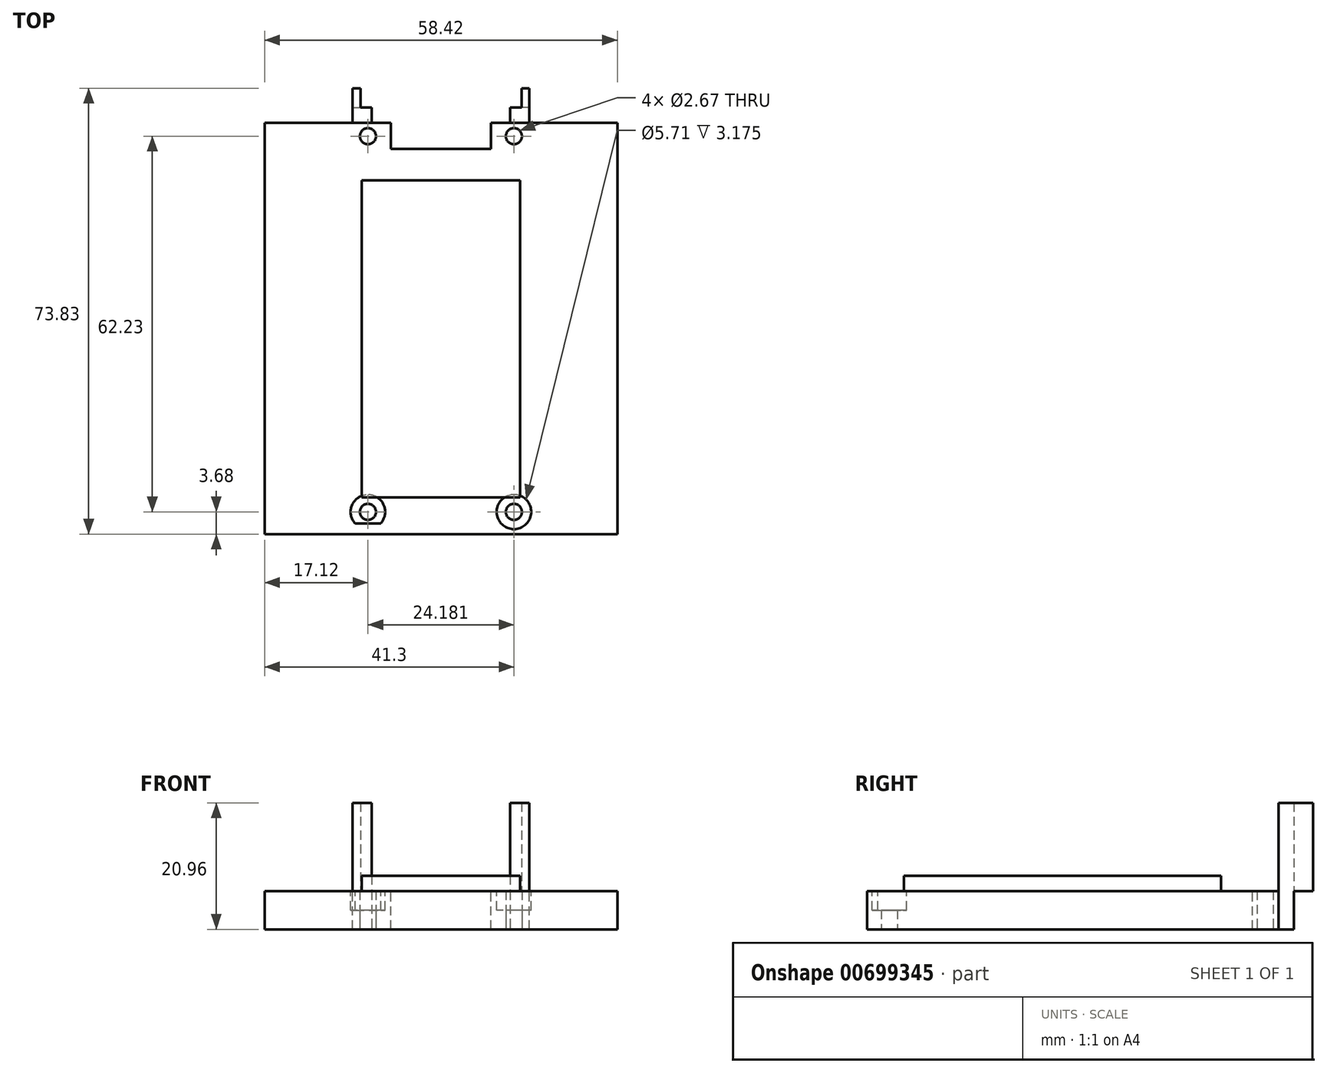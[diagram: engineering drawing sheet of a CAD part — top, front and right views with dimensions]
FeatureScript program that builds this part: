
annotation { "Feature Type Name" : "Feature", "Feature Type Description" : "" }
export const myFeature = defineFeature(function(context is Context, id is Id, definition is map)
    precondition{}
    {
        {
            var Q0;
            Q0=qCreatedBy(makeId("Top.planeOp"),FACE);
            var sketch = newSketch(context, id + "F0", { "sketchPlane" : qUnion([Q0])});
            skLineSegment(sketch, "E0.bottom", {"start": v(0, 0) * mm, "end": v(58.42, 0) * mm});
            skLineSegment(sketch, "E0.top", {"start": v(0, -66.34) * mm, "end": v(58.42, -66.34) * mm});
            skLineSegment(sketch, "E0.left", {"start": v(0, 0) * mm, "end": v(0, -66.34) * mm});
            skLineSegment(sketch, "E0.right", {"start": v(58.42, 0) * mm, "end": v(58.42, -66.34) * mm});
            skCircle(sketch, "E1", {"center": v(41.3, -64.44) * mm, "radius": 1.33 * mm});
            skCircle(sketch, "E2", {"center": v(17.12, -64.44) * mm, "radius": 1.33 * mm});
            skCircle(sketch, "E3", {"center": v(41.3, -2.2) * mm, "radius": 1.33 * mm});
            skCircle(sketch, "E4", {"center": v(17.12, -2.2) * mm, "radius": 1.33 * mm});
            skCircle(sketch, "E5", {"center": v(17.12, -64.44) * mm, "radius": 2.86 * mm});
            skCircle(sketch, "E6", {"center": v(41.3, -64.44) * mm, "radius": 2.86 * mm});
            skSolve(sketch);
        }
        {
            var Q0;
            Q0=makeQuery(id+"F0.imprint","IMPRINT",FACE,{"disambiguationData":[TD([[makeQuery(id+"F0.imprint","IMPRINT",EDGE,{"derivedFrom":sQuery(id+"F0.wireOp",EDGE,"E0.bottom")}),-1.0]])]});
            var Q1;
            Q1=makeQuery(id+"F0.imprint","IMPRINT",FACE,{"disambiguationData":[TD([[makeQuery(id+"F0.imprint","IMPRINT",EDGE,{"derivedFrom":sQuery(id+"F0.wireOp",EDGE,"E2")}),-1.0]])]});
            var Q2;
            Q2=makeQuery(id+"F0.imprint","IMPRINT",FACE,{"disambiguationData":[TD([[makeQuery(id+"F0.imprint","IMPRINT",EDGE,{"derivedFrom":sQuery(id+"F0.wireOp",EDGE,"E1")}),-1.0]])]});
            extrude(context, id + "F1", {"entities" : qUnion([Q0, Q1, Q2]), "depth" : 6.35 * mm, "offsetDistance" : 25.4 * mm});
        }
        {
            var Q0;
            Q0=makeQuery(id+"F1.opExtrude","CAP_FACE",FACE,{"disambiguationData":[OSD([sQuery(id+"F0.wireOp",EDGE,"E0.bottom"),sQuery(id+"F0.wireOp",EDGE,"E0.top"),sQuery(id+"F0.wireOp",EDGE,"E0.left"),sQuery(id+"F0.wireOp",EDGE,"E0.right"),sQuery(id+"F0.wireOp",EDGE,"E1"),sQuery(id+"F0.wireOp",EDGE,"E2"),sQuery(id+"F0.wireOp",EDGE,"E3"),sQuery(id+"F0.wireOp",EDGE,"E4")])],"isStart":false});
            var sketch = newSketch(context, id + "F2", { "sketchPlane" : qUnion([Q0])});
            skLineSegment(sketch, "E7.bottom", {"start": v(37.46, -4.32) * mm, "end": v(20.96, -4.32) * mm});
            skLineSegment(sketch, "E7.top", {"start": v(37.46, 0) * mm, "end": v(20.96, 0) * mm});
            skLineSegment(sketch, "E7.left", {"start": v(37.46, -4.32) * mm, "end": v(37.46, 0) * mm});
            skLineSegment(sketch, "E7.right", {"start": v(20.96, -4.32) * mm, "end": v(20.96, 0) * mm});
            skLineSegment(sketch, "E8.bottom", {"start": v(0, 0) * mm, "end": v(20.96, 0) * mm});
            skLineSegment(sketch, "E8.top", {"start": v(0, -4.32) * mm, "end": v(20.96, -4.32) * mm});
            skLineSegment(sketch, "E8.left", {"start": v(0, 0) * mm, "end": v(0, -4.32) * mm});
            skLineSegment(sketch, "E8.right", {"start": v(20.96, 0) * mm, "end": v(20.96, -4.32) * mm});
            skLineSegment(sketch, "E9.bottom", {"start": v(37.46, 0) * mm, "end": v(58.42, 0) * mm});
            skLineSegment(sketch, "E9.top", {"start": v(37.46, -4.32) * mm, "end": v(58.42, -4.32) * mm});
            skLineSegment(sketch, "E9.left", {"start": v(37.46, 0) * mm, "end": v(37.46, -4.32) * mm});
            skLineSegment(sketch, "E9.right", {"start": v(58.42, 0) * mm, "end": v(58.42, -4.32) * mm});
            skLineSegment(sketch, "E10.bottom", {"start": v(20.96, 0) * mm, "end": v(13.3, 0) * mm});
            skLineSegment(sketch, "E10.top", {"start": v(20.96, -4.32) * mm, "end": v(13.3, -4.32) * mm});
            skLineSegment(sketch, "E10.right", {"start": v(13.3, 0) * mm, "end": v(13.3, -4.32) * mm});
            skLineSegment(sketch, "E11.bottom", {"start": v(37.46, 0) * mm, "end": v(45.12, 0) * mm});
            skLineSegment(sketch, "E11.top", {"start": v(37.46, -4.32) * mm, "end": v(45.12, -4.32) * mm});
            skLineSegment(sketch, "E11.right", {"start": v(45.12, 0) * mm, "end": v(45.12, -4.32) * mm});
            skLineSegment(sketch, "E12.bottom", {"start": v(20.96, 0) * mm, "end": v(19.56, 0) * mm});
            skLineSegment(sketch, "E12.top", {"start": v(20.96, -4.32) * mm, "end": v(19.56, -4.32) * mm});
            skLineSegment(sketch, "E12.right", {"start": v(19.56, 0) * mm, "end": v(19.56, -4.32) * mm});
            skLineSegment(sketch, "E13.bottom", {"start": v(37.46, 0) * mm, "end": v(38.86, 0) * mm});
            skLineSegment(sketch, "E13.top", {"start": v(37.46, -4.32) * mm, "end": v(38.86, -4.32) * mm});
            skLineSegment(sketch, "E13.right", {"start": v(38.86, 0) * mm, "end": v(38.86, -4.32) * mm});
            skSolve(sketch);
        }
        {
            var Q0;
            Q0=makeQuery(id+"F2.imprint","IMPRINT",FACE,{"disambiguationData":[TD([[makeQuery(id+"F2.imprint","IMPRINT",EDGE,{"derivedFrom":sQuery(id+"F2.wireOp",EDGE,"E7.bottom")}),-1.0]])]});
            extrude(context, id + "F3", {"entities" : qUnion([Q0]), "operationType" : NewBodyOperationType.REMOVE, "endBound" : BoundingType.THROUGH_ALL, "oppositeDirection" : true, "depth" : 25.4 * mm, "offsetDistance" : 25.4 * mm});
        }
        {
            var Q0;
            Q0=makeQuery(id+"F1.opExtrude","CAP_FACE",FACE,{"disambiguationData":[OSD([sQuery(id+"F0.wireOp",EDGE,"E0.bottom"),sQuery(id+"F0.wireOp",EDGE,"E0.top"),sQuery(id+"F0.wireOp",EDGE,"E0.left"),sQuery(id+"F0.wireOp",EDGE,"E0.right"),sQuery(id+"F0.wireOp",EDGE,"E1"),sQuery(id+"F0.wireOp",EDGE,"E2"),sQuery(id+"F0.wireOp",EDGE,"E3"),sQuery(id+"F0.wireOp",EDGE,"E4")])],"isStart":false});
            var sketch = newSketch(context, id + "F4", { "sketchPlane" : qUnion([Q0])});
            skLineSegment(sketch, "E14.bottom", {"start": v(16.13, -4.32) * mm, "end": v(42.3, -4.32) * mm});
            skLineSegment(sketch, "E14.top", {"start": v(16.13, -62.03) * mm, "end": v(42.3, -62.03) * mm});
            skLineSegment(sketch, "E14.left", {"start": v(16.13, -4.32) * mm, "end": v(16.13, -62.03) * mm});
            skLineSegment(sketch, "E14.right", {"start": v(42.3, -4.32) * mm, "end": v(42.3, -62.03) * mm});
            skLineSegment(sketch, "E15.bottom", {"start": v(16.13, -4.32) * mm, "end": v(21.34, -4.32) * mm});
            skLineSegment(sketch, "E15.top", {"start": v(16.13, -62.03) * mm, "end": v(21.34, -62.03) * mm});
            skLineSegment(sketch, "E15.right", {"start": v(21.34, -4.32) * mm, "end": v(21.34, -62.03) * mm});
            skLineSegment(sketch, "E16.top", {"start": v(16.13, -9.52) * mm, "end": v(42.3, -9.52) * mm});
            skLineSegment(sketch, "E16.left", {"start": v(16.13, -4.32) * mm, "end": v(16.13, -9.52) * mm});
            skLineSegment(sketch, "E16.right", {"start": v(42.3, -4.32) * mm, "end": v(42.3, -9.52) * mm});
            skLineSegment(sketch, "E17.bottom", {"start": v(42.3, -4.32) * mm, "end": v(37.08, -4.32) * mm});
            skLineSegment(sketch, "E17.top", {"start": v(42.3, -62.03) * mm, "end": v(37.08, -62.03) * mm});
            skLineSegment(sketch, "E17.right", {"start": v(37.08, -4.32) * mm, "end": v(37.08, -62.03) * mm});
            skSolve(sketch);
        }
        {
            var Q0;
            Q0=makeQuery(id+"F1.opExtrude","SWEPT_FACE",FACE,{"disambiguationData":[OSD([sQuery(id+"F0.wireOp",EDGE,"E0.top")])]});
            extrude(context, id + "F5", {"entities" : qUnion([Q0]), "operationType" : NewBodyOperationType.ADD, "depth" : 1.78 * mm, "offsetDistance" : 25.4 * mm});
        }
        {
            var Q0;
            Q0=makeQuery(id+"F0.imprint","IMPRINT",FACE,{"disambiguationData":[TD([[makeQuery(id+"F0.imprint","IMPRINT",EDGE,{"derivedFrom":sQuery(id+"F0.wireOp",EDGE,"E1")}),-1.0]])]});
            var Q1;
            Q1=makeQuery(id+"F0.imprint","IMPRINT",FACE,{"disambiguationData":[TD([[makeQuery(id+"F0.imprint","IMPRINT",EDGE,{"derivedFrom":sQuery(id+"F0.wireOp",EDGE,"E2")}),-1.0]])]});
            var Q2;
            {var subQ0=sQuery(id+"F0.wireOp",EDGE,"E5");var subQ1=sQuery(id+"F0.wireOp",EDGE,"E0.top");var subQ2=makeQuery(id+"F0.imprint","INTERSECT",VERTEX,{"disambiguationData":[OD(0.0)],"derivedFrom":[subQ1,subQ0]});Q2=makeQuery(id+"F0.imprint","IMPRINT",FACE,{"disambiguationData":[TD([[makeQuery(id+"F0.imprint","IMPRINT",EDGE,{"disambiguationData":[TD([[subQ2,-1.0]])],"derivedFrom":subQ1}),-1.0]])]});}
            var Q3;
            {var subQ0=sQuery(id+"F0.wireOp",EDGE,"E6");var subQ1=sQuery(id+"F0.wireOp",EDGE,"E0.top");var subQ2=makeQuery(id+"F0.imprint","INTERSECT",VERTEX,{"disambiguationData":[OD(0.0)],"derivedFrom":[subQ1,subQ0]});Q3=makeQuery(id+"F0.imprint","IMPRINT",FACE,{"disambiguationData":[TD([[makeQuery(id+"F0.imprint","IMPRINT",EDGE,{"disambiguationData":[TD([[subQ2,-1.0]])],"derivedFrom":subQ1}),-1.0]])]});}
            extrude(context, id + "F6", {"entities" : qUnion([Q0, Q1, Q2, Q3]), "operationType" : NewBodyOperationType.ADD, "depth" : 6.6 * mm, "offsetDistance" : 25.4 * mm});
        }
        {
            var Q0;
            Q0=makeQuery(id+"F6.opExtrude","CAP_FACE",FACE,{"disambiguationData":[OSD([sQuery(id+"F0.wireOp",EDGE,"E2"),sQuery(id+"F0.wireOp",EDGE,"E5")])],"isStart":false});
            var Q1;
            Q1=makeQuery(id+"F6.opExtrude","CAP_FACE",FACE,{"disambiguationData":[OSD([sQuery(id+"F0.wireOp",EDGE,"E1"),sQuery(id+"F0.wireOp",EDGE,"E6")])],"isStart":false});
            extrude(context, id + "F7", {"entities" : qUnion([Q0, Q1]), "operationType" : NewBodyOperationType.REMOVE, "oppositeDirection" : true, "depth" : 3.43 * mm, "offsetDistance" : 25.4 * mm});
        }
        {
            var Q0;
            {var subQ0=sQuery(id+"F4.wireOp",EDGE,"E14.top");Q0=makeQuery(id+"F4.imprint","IMPRINT",FACE,{"disambiguationData":[TD([[makeQuery(id+"F4.imprint","IMPRINT",EDGE,{"derivedFrom":subQ0}),1.0]])]});}
            extrude(context, id + "F8", {"entities" : qUnion([Q0]), "operationType" : NewBodyOperationType.ADD, "depth" : 2.54 * mm, "offsetDistance" : 25.4 * mm});
        }
        {
            var Q0;
            {var subQ5=sQuery(id+"F0.wireOp",EDGE,"E0.left");var subQ7=sQuery(id+"F0.wireOp",EDGE,"E0.bottom");Q0=makeQuery(id+"F3.boolean.opBoolean","SPLIT",FACE,{"disambiguationData":[TD([makeQuery(id+"F1.opExtrude","SWEPT_FACE",FACE,{"disambiguationData":[OSD([subQ5])]})])],"derivedFrom":makeQuery(id+"F1.opExtrude","SWEPT_FACE",FACE,{"disambiguationData":[OSD([subQ7])]})});}
            var sketch = newSketch(context, id + "F9", { "sketchPlane" : qUnion([Q0])});
            skLineSegment(sketch, "E18.bottom", {"start": v(-20.96, 0) * mm, "end": v(-14.6, 0) * mm});
            skLineSegment(sketch, "E18.top", {"start": v(-20.96, 6.35) * mm, "end": v(-14.6, 6.35) * mm});
            skLineSegment(sketch, "E18.left", {"start": v(-20.96, 0) * mm, "end": v(-20.96, 6.35) * mm});
            skLineSegment(sketch, "E18.right", {"start": v(-14.6, 0) * mm, "end": v(-14.6, 6.35) * mm});
            skSolve(sketch);
        }
        {
            var Q0;
            {var subQ4=sQuery(id+"F0.wireOp",EDGE,"E0.right");var subQ7=sQuery(id+"F0.wireOp",EDGE,"E0.bottom");Q0=makeQuery(id+"F3.boolean.opBoolean","SPLIT",FACE,{"disambiguationData":[TD([makeQuery(id+"F1.opExtrude","SWEPT_FACE",FACE,{"disambiguationData":[OSD([subQ4])]})])],"derivedFrom":makeQuery(id+"F1.opExtrude","SWEPT_FACE",FACE,{"disambiguationData":[OSD([subQ7])]})});}
            var sketch = newSketch(context, id + "F10", { "sketchPlane" : qUnion([Q0])});
            skLineSegment(sketch, "E19.bottom", {"start": v(-37.46, 0) * mm, "end": v(-43.81, 0) * mm});
            skLineSegment(sketch, "E19.top", {"start": v(-37.46, 6.35) * mm, "end": v(-43.81, 6.35) * mm});
            skLineSegment(sketch, "E19.left", {"start": v(-37.46, 0) * mm, "end": v(-37.46, 6.35) * mm});
            skLineSegment(sketch, "E19.right", {"start": v(-43.81, 0) * mm, "end": v(-43.81, 6.35) * mm});
            skSolve(sketch);
        }
        {
            var Q0;
            Q0=makeQuery(id+"F9.imprint","IMPRINT",FACE,{"disambiguationData":[TD([[makeQuery(id+"F9.imprint","IMPRINT",EDGE,{"derivedFrom":sQuery(id+"F9.wireOp",EDGE,"E18.bottom")}),-1.0]])]});
            var Q1;
            Q1=makeQuery(id+"F10.imprint","IMPRINT",FACE,{"disambiguationData":[TD([[makeQuery(id+"F10.imprint","IMPRINT",EDGE,{"derivedFrom":sQuery(id+"F10.wireOp",EDGE,"E19.bottom")}),-1.0]])]});
            extrude(context, id + "F11", {"entities" : qUnion([Q0, Q1]), "operationType" : NewBodyOperationType.ADD, "depth" : 2.54 * mm, "offsetDistance" : 25.4 * mm});
        }
        {
            var Q0;
            {var subQ0=sQuery(id+"F0.wireOp",EDGE,"E0.top");Q0=makeQuery(id+"F11.boolean.opBoolean","MERGE",FACE,{"derivedFrom":[makeQuery(id+"F5.boolean.opBoolean","MERGE",FACE,{"derivedFrom":[makeQuery(id+"F1.opExtrude","CAP_FACE",FACE,{"disambiguationData":[OSD([sQuery(id+"F0.wireOp",EDGE,"E0.bottom"),subQ0,sQuery(id+"F0.wireOp",EDGE,"E0.left"),sQuery(id+"F0.wireOp",EDGE,"E0.right"),sQuery(id+"F0.wireOp",EDGE,"E1"),sQuery(id+"F0.wireOp",EDGE,"E2"),sQuery(id+"F0.wireOp",EDGE,"E3"),sQuery(id+"F0.wireOp",EDGE,"E4")])],"isStart":false}),makeQuery(id+"F5.opExtrude","SWEPT_FACE",FACE,{"disambiguationData":[OSD([subQ0]),TDD([makeQuery(id+"F1.opExtrude","CAP_EDGE",EDGE,{"disambiguationData":[OSD([subQ0])],"isStart":false})])]})]}),makeQuery(id+"F11.opExtrude","SWEPT_FACE",FACE,{"disambiguationData":[OSD([sQuery(id+"F9.wireOp",EDGE,"E18.top")])]}),makeQuery(id+"F11.opExtrude","SWEPT_FACE",FACE,{"disambiguationData":[OSD([sQuery(id+"F10.wireOp",EDGE,"E19.top")])]})]});}
            var sketch = newSketch(context, id + "F12", { "sketchPlane" : qUnion([Q0])});
            skLineSegment(sketch, "E20.bottom", {"start": v(14.6, 2.54) * mm, "end": v(20.96, 2.54) * mm});
            skLineSegment(sketch, "E20.top", {"start": v(14.6, 0) * mm, "end": v(20.96, 0) * mm});
            skLineSegment(sketch, "E20.left", {"start": v(14.6, 2.54) * mm, "end": v(14.6, 0) * mm});
            skLineSegment(sketch, "E20.right", {"start": v(20.96, 2.54) * mm, "end": v(20.96, 0) * mm});
            skLineSegment(sketch, "E21.bottom", {"start": v(37.46, 2.54) * mm, "end": v(43.81, 2.54) * mm});
            skLineSegment(sketch, "E21.top", {"start": v(37.46, 0) * mm, "end": v(43.81, 0) * mm});
            skLineSegment(sketch, "E21.left", {"start": v(37.46, 2.54) * mm, "end": v(37.46, 0) * mm});
            skLineSegment(sketch, "E21.right", {"start": v(43.81, 2.54) * mm, "end": v(43.81, 0) * mm});
            skSolve(sketch);
        }
        {
            var Q0;
            Q0=qSketchRegion(id+"F12",true);
            extrude(context, id + "F13", {"entities" : qUnion([Q0]), "operationType" : NewBodyOperationType.ADD, "depth" : 14.6 * mm, "offsetDistance" : 25.4 * mm});
        }
        {
            var Q0;
            {var subQ0=sQuery(id+"F0.wireOp",EDGE,"E0.top");Q0=makeQuery(id+"F11.boolean.opBoolean","MERGE",FACE,{"derivedFrom":[makeQuery(id+"F5.boolean.opBoolean","MERGE",FACE,{"derivedFrom":[makeQuery(id+"F1.opExtrude","CAP_FACE",FACE,{"disambiguationData":[OSD([sQuery(id+"F0.wireOp",EDGE,"E0.bottom"),subQ0,sQuery(id+"F0.wireOp",EDGE,"E0.left"),sQuery(id+"F0.wireOp",EDGE,"E0.right"),sQuery(id+"F0.wireOp",EDGE,"E1"),sQuery(id+"F0.wireOp",EDGE,"E2"),sQuery(id+"F0.wireOp",EDGE,"E3"),sQuery(id+"F0.wireOp",EDGE,"E4")])],"isStart":true}),makeQuery(id+"F5.opExtrude","SWEPT_FACE",FACE,{"disambiguationData":[OSD([subQ0]),TDD([makeQuery(id+"F1.opExtrude","CAP_EDGE",EDGE,{"disambiguationData":[OSD([subQ0])],"isStart":true})])]})]}),makeQuery(id+"F11.opExtrude","SWEPT_FACE",FACE,{"disambiguationData":[OSD([sQuery(id+"F9.wireOp",EDGE,"E18.bottom")])]}),makeQuery(id+"F11.opExtrude","SWEPT_FACE",FACE,{"disambiguationData":[OSD([sQuery(id+"F10.wireOp",EDGE,"E19.bottom")])]})]});}
            var sketch = newSketch(context, id + "F14", { "sketchPlane" : qUnion([Q0])});
            skLineSegment(sketch, "E22.bottom", {"start": v(20.96, -2.54) * mm, "end": v(17.78, -2.54) * mm});
            skLineSegment(sketch, "E22.top", {"start": v(20.96, 0) * mm, "end": v(17.78, 0) * mm});
            skLineSegment(sketch, "E22.left", {"start": v(20.96, -2.54) * mm, "end": v(20.96, 0) * mm});
            skLineSegment(sketch, "E22.right", {"start": v(17.78, -2.54) * mm, "end": v(17.78, 0) * mm});
            skLineSegment(sketch, "E23.bottom", {"start": v(37.46, -2.54) * mm, "end": v(40.64, -2.54) * mm});
            skLineSegment(sketch, "E23.top", {"start": v(37.46, 0) * mm, "end": v(40.64, 0) * mm});
            skLineSegment(sketch, "E23.left", {"start": v(37.46, -2.54) * mm, "end": v(37.46, 0) * mm});
            skLineSegment(sketch, "E23.right", {"start": v(40.64, -2.54) * mm, "end": v(40.64, 0) * mm});
            skSolve(sketch);
        }
        {
            var Q0;
            Q0=makeQuery(id+"F14.imprint","IMPRINT",FACE,{"disambiguationData":[TD([[makeQuery(id+"F14.imprint","IMPRINT",EDGE,{"derivedFrom":sQuery(id+"F14.wireOp",EDGE,"E22.bottom")}),1.0]])]});
            var Q1;
            Q1=makeQuery(id+"F14.imprint","IMPRINT",FACE,{"disambiguationData":[TD([[makeQuery(id+"F14.imprint","IMPRINT",EDGE,{"derivedFrom":sQuery(id+"F14.wireOp",EDGE,"E23.bottom")}),1.0]])]});
            extrude(context, id + "F15", {"entities" : qUnion([Q0, Q1]), "operationType" : NewBodyOperationType.REMOVE, "endBound" : BoundingType.THROUGH_ALL, "oppositeDirection" : true, "depth" : 25.4 * mm, "offsetDistance" : 25.4 * mm});
        }
        {
            var Q0;
            Q0=makeQuery(id+"F13.boolean.opBoolean","MERGE",FACE,{"derivedFrom":[makeQuery(id+"F11.opExtrude","CAP_FACE",FACE,{"disambiguationData":[OSD([sQuery(id+"F10.wireOp",EDGE,"E19.bottom"),sQuery(id+"F10.wireOp",EDGE,"E19.top"),sQuery(id+"F10.wireOp",EDGE,"E19.left"),sQuery(id+"F10.wireOp",EDGE,"E19.right")])],"isStart":false}),makeQuery(id+"F13.opExtrude","SWEPT_FACE",FACE,{"disambiguationData":[OSD([sQuery(id+"F12.wireOp",EDGE,"E21.bottom")])]})]});
            var sketch = newSketch(context, id + "F16", { "sketchPlane" : qUnion([Q0])});
            skLineSegment(sketch, "E24.bottom", {"start": v(-43.81, 20.96) * mm, "end": v(-42.54, 20.96) * mm});
            skLineSegment(sketch, "E24.top", {"start": v(-43.81, 6.35) * mm, "end": v(-42.54, 6.35) * mm});
            skLineSegment(sketch, "E24.left", {"start": v(-43.81, 20.96) * mm, "end": v(-43.81, 6.35) * mm});
            skLineSegment(sketch, "E24.right", {"start": v(-42.54, 20.96) * mm, "end": v(-42.54, 6.35) * mm});
            skSolve(sketch);
        }
        {
            var Q0;
            Q0=makeQuery(id+"F13.boolean.opBoolean","MERGE",FACE,{"derivedFrom":[makeQuery(id+"F11.opExtrude","CAP_FACE",FACE,{"disambiguationData":[OSD([sQuery(id+"F9.wireOp",EDGE,"E18.bottom"),sQuery(id+"F9.wireOp",EDGE,"E18.top"),sQuery(id+"F9.wireOp",EDGE,"E18.left"),sQuery(id+"F9.wireOp",EDGE,"E18.right")])],"isStart":false}),makeQuery(id+"F13.opExtrude","SWEPT_FACE",FACE,{"disambiguationData":[OSD([sQuery(id+"F12.wireOp",EDGE,"E20.bottom")])]})]});
            var sketch = newSketch(context, id + "F17", { "sketchPlane" : qUnion([Q0])});
            skLineSegment(sketch, "E25.bottom", {"start": v(-14.6, 20.96) * mm, "end": v(-15.88, 20.96) * mm});
            skLineSegment(sketch, "E25.top", {"start": v(-14.6, 6.35) * mm, "end": v(-15.87, 6.35) * mm});
            skLineSegment(sketch, "E25.left", {"start": v(-14.6, 20.96) * mm, "end": v(-14.6, 6.35) * mm});
            skLineSegment(sketch, "E25.right", {"start": v(-15.88, 20.96) * mm, "end": v(-15.88, 6.35) * mm});
            skSolve(sketch);
        }
        {
            var Q0;
            Q0=makeQuery(id+"F16.imprint","IMPRINT",FACE,{"disambiguationData":[TD([[makeQuery(id+"F16.imprint","IMPRINT",EDGE,{"derivedFrom":sQuery(id+"F16.wireOp",EDGE,"E24.bottom")}),1.0]])]});
            var Q1;
            Q1=makeQuery(id+"F17.imprint","IMPRINT",FACE,{"disambiguationData":[TD([[makeQuery(id+"F17.imprint","IMPRINT",EDGE,{"derivedFrom":sQuery(id+"F17.wireOp",EDGE,"E25.bottom")}),1.0]])]});
            extrude(context, id + "F18", {"entities" : qUnion([Q0, Q1]), "operationType" : NewBodyOperationType.ADD, "depth" : 3.17 * mm, "offsetDistance" : 25.4 * mm});
        }
    });
